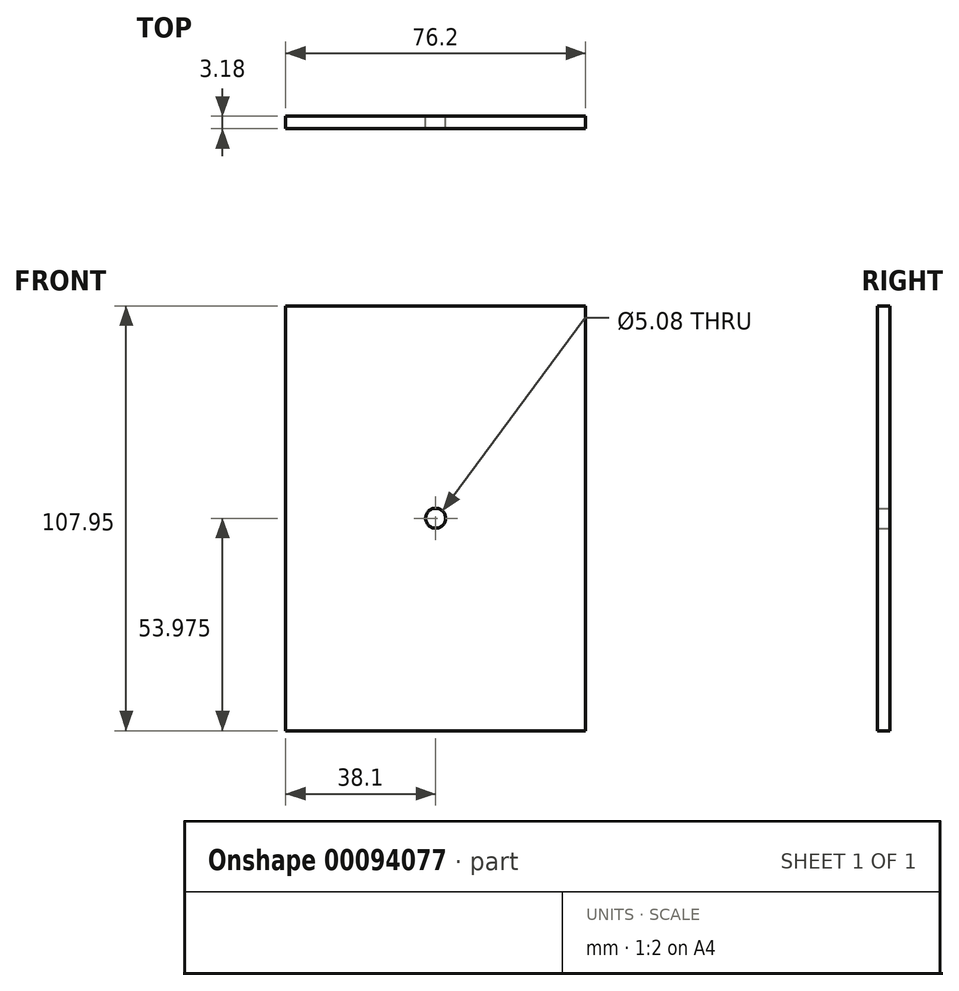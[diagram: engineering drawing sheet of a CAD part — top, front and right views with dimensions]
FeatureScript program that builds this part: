
annotation { "Feature Type Name" : "Feature", "Feature Type Description" : "" }
export const myFeature = defineFeature(function(context is Context, id is Id, definition is map)
    precondition{}
    {
        {
            var Q0;
            Q0=qCreatedBy(makeId("Top.planeOp"),FACE);
            var sketch = newSketch(context, id + "F0", { "sketchPlane" : qUnion([Q0])});
            skLineSegment(sketch, "E0.bottom", {"start": v(0, 0) * mm, "end": v(76.2, 0) * mm});
            skLineSegment(sketch, "E0.top", {"start": v(0, 3.18) * mm, "end": v(76.2, 3.18) * mm});
            skLineSegment(sketch, "E0.left", {"start": v(0, 0) * mm, "end": v(0, 3.17) * mm});
            skLineSegment(sketch, "E0.right", {"start": v(76.2, 0) * mm, "end": v(76.2, 3.18) * mm});
            skLineSegment(sketch, "E1.bottom", {"start": v(76.2, 0) * mm, "end": v(73.02, 0) * mm});
            skLineSegment(sketch, "E1.top", {"start": v(76.2, -104.77) * mm, "end": v(73.03, -104.77) * mm});
            skLineSegment(sketch, "E1.left", {"start": v(76.2, 0) * mm, "end": v(76.2, -104.77) * mm});
            skLineSegment(sketch, "E1.right", {"start": v(73.02, 0) * mm, "end": v(73.03, -104.77) * mm});
            skSolve(sketch);
        }
        {
            var Q0;
            Q0=makeQuery(id+"F0.imprint","IMPRINT",FACE,{"disambiguationData":[TD([[makeQuery(id+"F0.imprint","IMPRINT",EDGE,{"derivedFrom":sQuery(id+"F0.wireOp",EDGE,"E0.bottom")}),1.0]])]});
            var Q1;
            Q1=makeQuery(id+"F0.imprint","IMPRINT",FACE,{"disambiguationData":[TD([[makeQuery(id+"F0.imprint","IMPRINT",EDGE,{"derivedFrom":sQuery(id+"F0.wireOp",EDGE,"E1.bottom")}),1.0]])]});
            extrude(context, id + "F1", {"entities" : qUnion([Q0, Q1]), "depth" : 107.95 * mm});
        }
        {
            var Q0;
            Q0=makeQuery(id+"F1.opExtrude","SWEPT_FACE",FACE,{"disambiguationData":[OSD([sQuery(id+"F0.wireOp",EDGE,"E0.top")])]});
            var sketch = newSketch(context, id + "F2", { "sketchPlane" : qUnion([Q0])});
            skPoint(sketch, "E2", {"position": v(-38.1, 0) * mm});
            skPoint(sketch, "E3", {"position": v(0, 53.98) * mm});
            skLineSegment(sketch, "E4", {"start": v(0, 53.98) * mm, "end": v(-76.2, 53.98) * mm, "construction": true});
            skLineSegment(sketch, "E5", {"start": v(-38.1, 0) * mm, "end": v(-38.1, 107.95) * mm, "construction": true});
            skCircle(sketch, "E6", {"center": v(-38.1, 53.98) * mm, "radius": 2.54 * mm});
            skSolve(sketch);
        }
        {
            var Q0;
            Q0=makeQuery(id+"F2.imprint","IMPRINT",FACE,{"disambiguationData":[TD([[makeQuery(id+"F2.imprint","IMPRINT",EDGE,{"derivedFrom":sQuery(id+"F2.wireOp",EDGE,"E6")}),1.0]])]});
            extrude(context, id + "F3", {"entities" : qUnion([Q0]), "operationType" : NewBodyOperationType.REMOVE, "oppositeDirection" : true, "depth" : 25.4 * mm});
        }
    });
